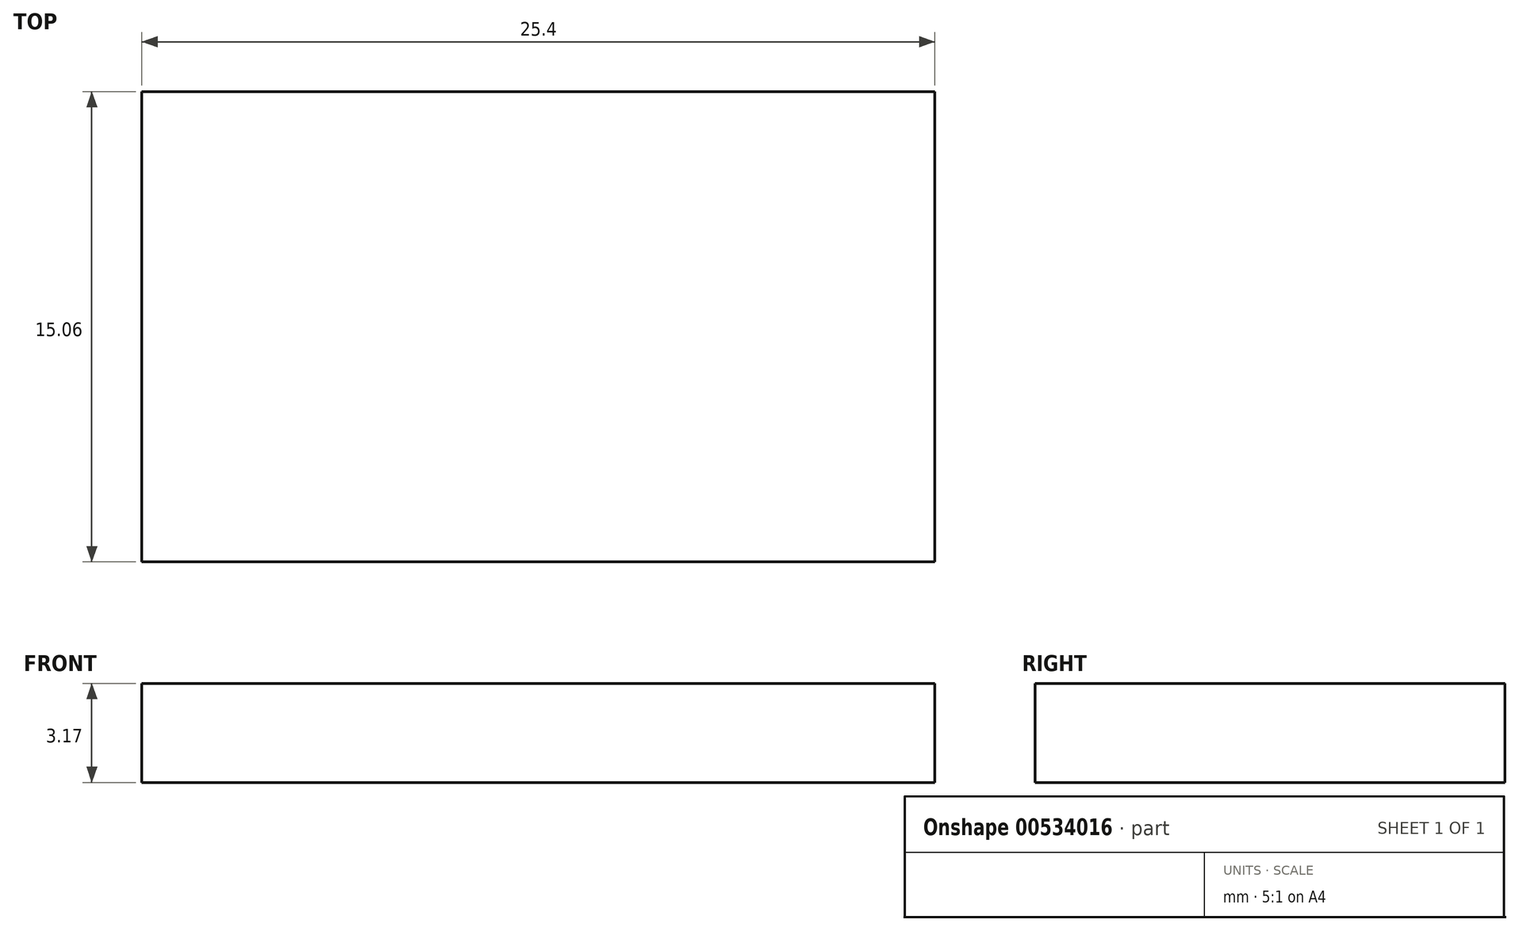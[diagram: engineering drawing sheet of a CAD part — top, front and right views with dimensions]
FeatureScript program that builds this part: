
annotation { "Feature Type Name" : "Feature", "Feature Type Description" : "" }
export const myFeature = defineFeature(function(context is Context, id is Id, definition is map)
    precondition{}
    {
        {
            var Q0;
            Q0=qCreatedBy(makeId("Top.planeOp"),FACE);
            var sketch = newSketch(context, id + "F0", { "sketchPlane" : qUnion([Q0])});
            skLineSegment(sketch, "E0.bottom", {"start": v(12.7, 7.53) * mm, "end": v(-12.7, 7.53) * mm});
            skLineSegment(sketch, "E0.top", {"start": v(12.7, -7.53) * mm, "end": v(-12.7, -7.53) * mm});
            skLineSegment(sketch, "E0.left", {"start": v(12.7, 7.53) * mm, "end": v(12.7, -7.53) * mm});
            skLineSegment(sketch, "E0.right", {"start": v(-12.7, 7.53) * mm, "end": v(-12.7, -7.53) * mm});
            skPoint(sketch, "E0.middle", {"position": v(0, 0) * mm});
            skSolve(sketch);
        }
        {
            var Q0;
            Q0 = qConstructionFilter(qBodyType(qCreatedBy(id + "F0" ,EDGE), BodyType.WIRE), ConstructionObject.NO);
            extrude(context, id + "F1", {"bodyType" : ToolBodyType.SURFACE, "surfaceEntities" : qUnion([Q0]), "depth" : 3.17 * mm, "offsetDistance" : 25.4 * mm});
        }
    });
